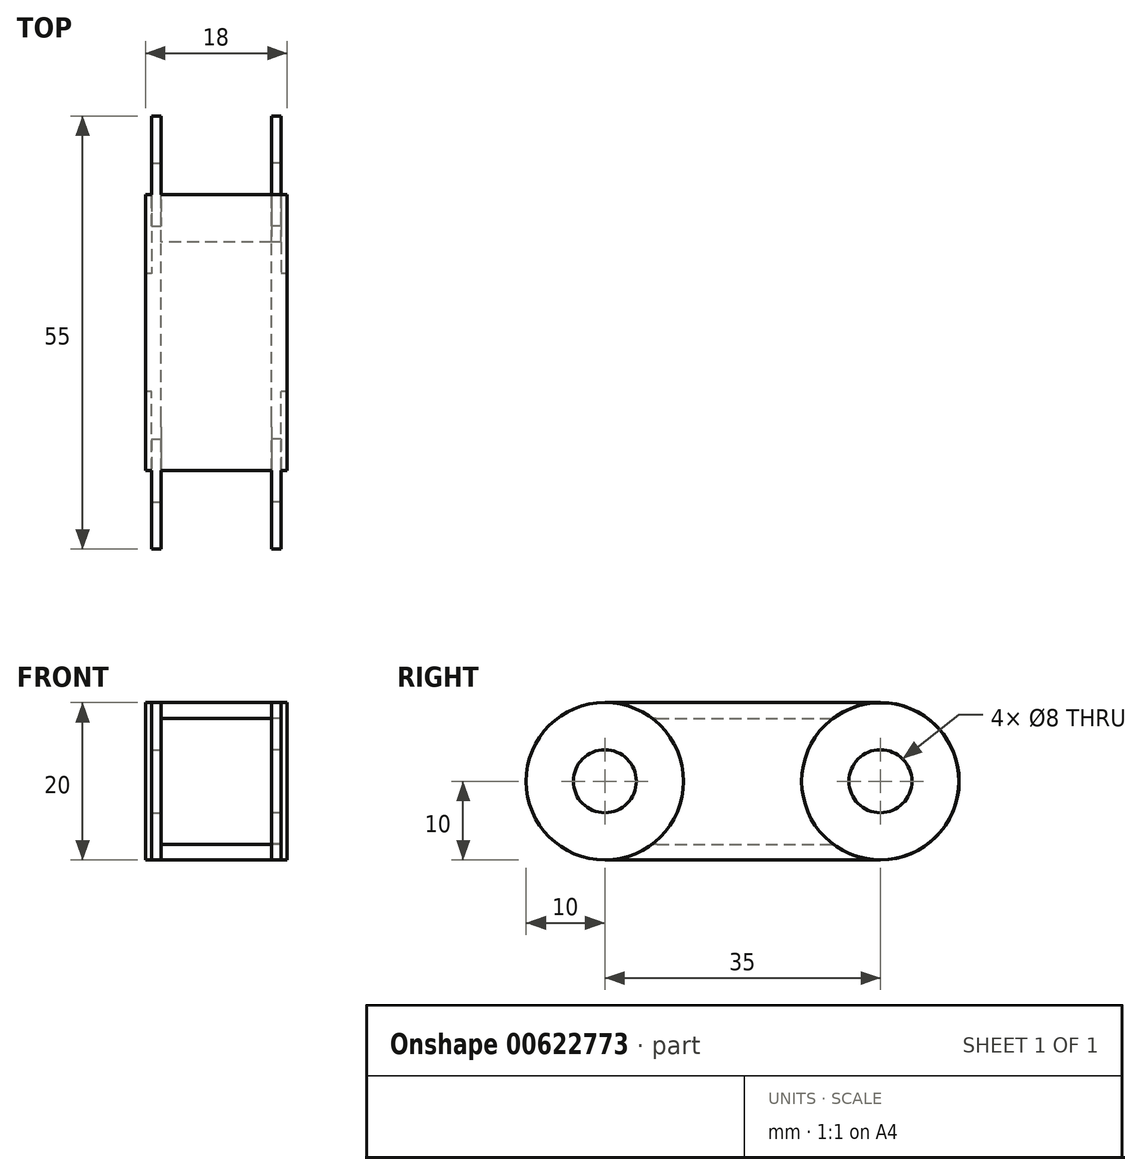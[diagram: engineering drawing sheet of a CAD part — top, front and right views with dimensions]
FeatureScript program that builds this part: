
annotation { "Feature Type Name" : "Feature", "Feature Type Description" : "" }
export const myFeature = defineFeature(function(context is Context, id is Id, definition is map)
    precondition{}
    {
        {
            var Q0;
            Q0=qCreatedBy(makeId("Right.planeOp"),FACE);
            var sketch = newSketch(context, id + "F0", { "sketchPlane" : qUnion([Q0])});
            skCircle(sketch, "E0", {"center": v(0, 0) * mm, "radius": 10 * mm});
            skCircle(sketch, "E1", {"center": v(0, 0) * mm, "radius": 4 * mm});
            skCircle(sketch, "E2", {"center": v(-35, 0) * mm, "radius": 10 * mm});
            skPoint(sketch, "E2.centerSnap0", {"position": v(-30, 0) * mm});
            skLineSegment(sketch, "E3", {"start": v(0, 10) * mm, "end": v(-35, 10) * mm});
            skLineSegment(sketch, "E4", {"start": v(0, -10) * mm, "end": v(-35, -10) * mm});
            skCircle(sketch, "E5", {"center": v(-35, 0) * mm, "radius": 4 * mm});
            skLineSegment(sketch, "E6", {"start": v(6, 8) * mm, "end": v(-29, 8) * mm});
            skLineSegment(sketch, "E7", {"start": v(-6, -8) * mm, "end": v(-29, -8) * mm});
            skSolve(sketch);
        }
        {
            var Q0;
            {var subQ0=sQuery(id+"F0.wireOp",EDGE,"E3");Q0=makeQuery(id+"F0.imprint","IMPRINT",FACE,{"disambiguationData":[TD([[makeQuery(id+"F0.imprint","IMPRINT",EDGE,{"derivedFrom":subQ0}),1.0]])]});}
            extrude(context, id + "F1", {"entities" : qUnion([Q0]), "depth" : 18 * mm, "offsetDistance" : 25 * mm});
        }
        {
            var Q0;
            Q0=makeQuery(id+"F1.opExtrude","SWEPT_FACE",FACE,{"disambiguationData":[OSD([sQuery(id+"F0.wireOp",EDGE,"E6")])]});
            var sketch = newSketch(context, id + "F2", { "sketchPlane" : qUnion([Q0])});
            skLineSegment(sketch, "E8.bottom", {"start": v(18, 29) * mm, "end": v(16, 29) * mm});
            skLineSegment(sketch, "E8.top", {"start": v(18, 6) * mm, "end": v(16, 6) * mm});
            skLineSegment(sketch, "E8.left", {"start": v(18, 29) * mm, "end": v(18, 6) * mm});
            skLineSegment(sketch, "E8.right", {"start": v(16, 29) * mm, "end": v(16, 6) * mm});
            skLineSegment(sketch, "E9", {"start": v(2, 29) * mm, "end": v(2, 6) * mm});
            skSolve(sketch);
        }
        {
            var Q0;
            Q0=makeQuery(id+"F2.imprint","IMPRINT",FACE,{"disambiguationData":[TD([[makeQuery(id+"F2.imprint","IMPRINT",EDGE,{"derivedFrom":sQuery(id+"F2.wireOp",EDGE,"E8.bottom")}),1.0]])]});
            var Q1;
            {var subQ0=sQuery(id+"F2.wireOp",EDGE,"E9");Q1=makeQuery(id+"F2.imprint","IMPRINT",FACE,{"disambiguationData":[TD([[makeQuery(id+"F2.imprint","IMPRINT",EDGE,{"derivedFrom":subQ0}),-1.0]])]});}
            extrude(context, id + "F3", {"entities" : qUnion([Q0, Q1]), "operationType" : NewBodyOperationType.ADD, "depth" : 18 * mm, "offsetDistance" : 25 * mm});
        }
        {
            var Q0;
            {var subQ0=sQuery(id+"F0.wireOp",EDGE,"E4");Q0=makeQuery(id+"F0.imprint","IMPRINT",FACE,{"disambiguationData":[TD([[makeQuery(id+"F0.imprint","IMPRINT",EDGE,{"derivedFrom":subQ0}),-1.0]])]});}
            extrude(context, id + "F4", {"entities" : qUnion([Q0]), "operationType" : NewBodyOperationType.ADD, "depth" : 18 * mm, "offsetDistance" : 25 * mm});
        }
        {
            var Q0;
            {var subQ0=sQuery(id+"F0.wireOp",EDGE,"E2");var subQ1=sQuery(id+"F0.wireOp",EDGE,"E7");Q0=makeQuery(id+"F4.boolean.opBoolean","SPLIT",EDGE,{"disambiguationData":[topologyDisambiguationEdgeConnected([makeQuery(id+"F4.opExtrude","SWEPT_FACE",FACE,{"disambiguationData":[OSD([subQ1])]})])],"derivedFrom":makeQuery(id+"F4.opExtrude","SWEPT_EDGE",EDGE,{"disambiguationData":[OSD([subQ0,subQ1])]})});}
            fillet(context, id + "F5", {"entities" : qUnion([Q0]), "radius" : 2 * mm, "tangentPropagation" : true, "allowEdgeOverflow" : false});
        }
        {
            var Q0;
            Q0=makeQuery(id+"F3.boolean.opBoolean","SPLIT",EDGE,{"derivedFrom":makeQuery(id+"F1.opExtrude","SWEPT_EDGE",EDGE,{"disambiguationData":[OSD([sQuery(id+"F0.wireOp",EDGE,"E2"),sQuery(id+"F0.wireOp",EDGE,"E6")])]})});
            fillet(context, id + "F6", {"entities" : qUnion([Q0]), "radius" : 2 * mm, "tangentPropagation" : true, "allowEdgeOverflow" : false});
        }
        {
            var Q0;
            Q0=makeQuery(id+"F3.opExtrude","SWEPT_EDGE",EDGE,{"disambiguationData":[OSD([sQuery(id+"F0.wireOp",EDGE,"E2"),sQuery(id+"F0.wireOp",EDGE,"E6"),sQuery(id+"F2.wireOp",EDGE,"E9")])]});
            var Q1;
            Q1=makeQuery(id+"F3.opExtrude","SWEPT_EDGE",EDGE,{"disambiguationData":[OSD([sQuery(id+"F0.wireOp",EDGE,"E2"),sQuery(id+"F0.wireOp",EDGE,"E6"),sQuery(id+"F2.wireOp",EDGE,"E8.bottom"),sQuery(id+"F2.wireOp",EDGE,"E8.right")])]});
            fillet(context, id + "F7", {"entities" : qUnion([Q0, Q1]), "radius" : 1 * mm, "tangentPropagation" : true, "allowEdgeOverflow" : false});
        }
        {
            var Q0;
            Q0=makeQuery(id+"F3.opExtrude","SWEPT_FACE",FACE,{"disambiguationData":[OSD([sQuery(id+"F2.wireOp",EDGE,"E9")])]});
            var sketch = newSketch(context, id + "F8", { "sketchPlane" : qUnion([Q0])});
            skCircle(sketch, "E10", {"center": v(-35, 0) * mm, "radius": 10 * mm});
            skCircle(sketch, "E11", {"center": v(-35, 0) * mm, "radius": 4 * mm});
            skCircle(sketch, "E12", {"center": v(0, 0) * mm, "radius": 10 * mm});
            skCircle(sketch, "E13", {"center": v(0, 0) * mm, "radius": 4 * mm});
            skSolve(sketch);
        }
        {
            var Q0;
            {var subQ1=sQuery(id+"F2.wireOp",EDGE,"E9");var subQ2=makeQuery(id+"F3.opExtrude","SWEPT_FACE",FACE,{"disambiguationData":[OSD([subQ1])]});var subQ3=subQ2;var subQ4=sQuery(id+"F0.wireOp",EDGE,"E6");var subQ5=sQuery(id+"F0.wireOp",EDGE,"E2");var subQ7=makeQuery(id+"F7.opFillet","BLEND_EDGE",EDGE,{"blendedFrom":[makeQuery(id+"F3.opExtrude","SWEPT_EDGE",EDGE,{"disambiguationData":[OSD([subQ5,subQ4,subQ1])]}),subQ3],"blendedInto":[subQ3]});Q0=makeQuery(id+"F8.imprint","IMPRINT",FACE,{"disambiguationData":[TD([[makeQuery(id+"F8.imprint","IMPRINT",EDGE,{"derivedFrom":subQ7}),-1.0]])]});}
            extrude(context, id + "F9", {"entities" : qUnion([Q0]), "operationType" : NewBodyOperationType.ADD, "oppositeDirection" : true, "depth" : 1.25 * mm, "offsetDistance" : 25 * mm});
        }
        {
            var Q0;
            {var subQ0=sQuery(id+"F0.wireOp",EDGE,"E2");var subQ1=sQuery(id+"F0.wireOp",EDGE,"E0");var subQ2=sQuery(id+"F0.wireOp",EDGE,"E6");Q0=makeQuery(id+"F4.boolean.opBoolean","MERGE",FACE,{"derivedFrom":[makeQuery(id+"F3.boolean.opBoolean","MERGE",FACE,{"derivedFrom":[makeQuery(id+"F1.opExtrude","CAP_FACE",FACE,{"disambiguationData":[OSD([subQ1,subQ0,sQuery(id+"F0.wireOp",EDGE,"E3"),subQ2])],"isStart":true}),makeQuery(id+"F3.opExtrude","SWEPT_FACE",FACE,{"disambiguationData":[OSD([subQ2])]})]}),makeQuery(id+"F4.opExtrude","CAP_FACE",FACE,{"disambiguationData":[OSD([subQ1,subQ0,sQuery(id+"F0.wireOp",EDGE,"E4"),sQuery(id+"F0.wireOp",EDGE,"E7")])],"isStart":true})]});}
            var sketch = newSketch(context, id + "F10", { "sketchPlane" : qUnion([Q0])});
            skArc(sketch, "E14", {"start": v(29, 8) * mm, "mid": v(25, 0) * mm, "end": v(29, -8) * mm});
            skArc(sketch, "E15", {"start": v(6, -8) * mm, "mid": v(10, 0) * mm, "end": v(6, 8) * mm});
            skSolve(sketch);
        }
        {
            var Q0;
            Q0=makeQuery(id+"F10.imprint","IMPRINT",FACE,{"disambiguationData":[TD([[makeQuery(id+"F10.imprint","IMPRINT",EDGE,{"derivedFrom":sQuery(id+"F10.wireOp",EDGE,"E14")}),1.0]])]});
            extrude(context, id + "F11", {"entities" : qUnion([Q0]), "operationType" : NewBodyOperationType.REMOVE, "oppositeDirection" : true, "depth" : 0.75 * mm, "offsetDistance" : 25 * mm});
        }
        {
            var Q0;
            Q0=makeQuery(id+"F8.imprint","IMPRINT",FACE,{"disambiguationData":[TD([[makeQuery(id+"F8.imprint","IMPRINT",EDGE,{"derivedFrom":sQuery(id+"F8.wireOp",EDGE,"E13")}),-1.0]])]});
            extrude(context, id + "F12", {"entities" : qUnion([Q0]), "operationType" : NewBodyOperationType.ADD, "oppositeDirection" : true, "depth" : 1.25 * mm, "offsetDistance" : 25 * mm});
        }
        {
            var Q0;
            Q0=makeQuery(id+"F10.imprint","IMPRINT",FACE,{"disambiguationData":[TD([[makeQuery(id+"F10.imprint","IMPRINT",EDGE,{"derivedFrom":sQuery(id+"F10.wireOp",EDGE,"E15")}),1.0]])]});
            extrude(context, id + "F13", {"entities" : qUnion([Q0]), "operationType" : NewBodyOperationType.REMOVE, "oppositeDirection" : true, "depth" : 0.75 * mm, "offsetDistance" : 25 * mm});
        }
        {
            var Q0;
            Q0=makeQuery(id+"F3.opExtrude","SWEPT_FACE",FACE,{"disambiguationData":[OSD([sQuery(id+"F2.wireOp",EDGE,"E8.right")])]});
            var sketch = newSketch(context, id + "F14", { "sketchPlane" : qUnion([Q0])});
            skCircle(sketch, "E16", {"center": v(0, 0) * mm, "radius": 4 * mm});
            skCircle(sketch, "E17", {"center": v(0, 0) * mm, "radius": 9.97 * mm});
            skCircle(sketch, "E18", {"center": v(0, 0) * mm, "radius": 10 * mm});
            skCircle(sketch, "E19", {"center": v(35, 0) * mm, "radius": 10 * mm});
            skCircle(sketch, "E20", {"center": v(35, 0) * mm, "radius": 4 * mm});
            skSolve(sketch);
        }
        {
            var Q0;
            Q0=makeQuery(id+"F14.imprint","IMPRINT",FACE,{"disambiguationData":[TD([[makeQuery(id+"F14.imprint","IMPRINT",EDGE,{"derivedFrom":sQuery(id+"F14.wireOp",EDGE,"E20")}),-1.0]])]});
            var Q1;
            Q1=makeQuery(id+"F14.imprint","IMPRINT",FACE,{"disambiguationData":[TD([[makeQuery(id+"F14.imprint","IMPRINT",EDGE,{"derivedFrom":sQuery(id+"F14.wireOp",EDGE,"E16")}),-1.0]])]});
            extrude(context, id + "F15", {"entities" : qUnion([Q0, Q1]), "operationType" : NewBodyOperationType.ADD, "oppositeDirection" : true, "depth" : 1.25 * mm, "offsetDistance" : 25 * mm});
        }
        {
            var Q0;
            {var subQ0=sQuery(id+"F0.wireOp",EDGE,"E2");var subQ1=sQuery(id+"F0.wireOp",EDGE,"E0");Q0=makeQuery(id+"F4.boolean.opBoolean","MERGE",FACE,{"derivedFrom":[makeQuery(id+"F3.boolean.opBoolean","MERGE",FACE,{"derivedFrom":[makeQuery(id+"F1.opExtrude","CAP_FACE",FACE,{"disambiguationData":[OSD([subQ1,subQ0,sQuery(id+"F0.wireOp",EDGE,"E3"),sQuery(id+"F0.wireOp",EDGE,"E6")])],"isStart":false}),makeQuery(id+"F3.opExtrude","SWEPT_FACE",FACE,{"disambiguationData":[OSD([sQuery(id+"F2.wireOp",EDGE,"E8.left")])]})]}),makeQuery(id+"F4.opExtrude","CAP_FACE",FACE,{"disambiguationData":[OSD([subQ1,subQ0,sQuery(id+"F0.wireOp",EDGE,"E4"),sQuery(id+"F0.wireOp",EDGE,"E7")])],"isStart":false})]});}
            var sketch = newSketch(context, id + "F16", { "sketchPlane" : qUnion([Q0])});
            skArc(sketch, "E21", {"start": v(-29, -8) * mm, "mid": v(-25, 0) * mm, "end": v(-29, 8) * mm});
            skArc(sketch, "E22", {"start": v(-6, 8) * mm, "mid": v(-10, 0) * mm, "end": v(-6, -8) * mm});
            skSolve(sketch);
        }
        {
            var Q0;
            Q0=makeQuery(id+"F16.imprint","IMPRINT",FACE,{"disambiguationData":[TD([[makeQuery(id+"F16.imprint","IMPRINT",EDGE,{"derivedFrom":sQuery(id+"F16.wireOp",EDGE,"E21")}),1.0]])]});
            var Q1;
            Q1=makeQuery(id+"F16.imprint","IMPRINT",FACE,{"disambiguationData":[TD([[makeQuery(id+"F16.imprint","IMPRINT",EDGE,{"derivedFrom":sQuery(id+"F16.wireOp",EDGE,"E22")}),1.0]])]});
            extrude(context, id + "F17", {"entities" : qUnion([Q0, Q1]), "operationType" : NewBodyOperationType.REMOVE, "oppositeDirection" : true, "depth" : 0.75 * mm, "offsetDistance" : 25 * mm});
        }
    });
